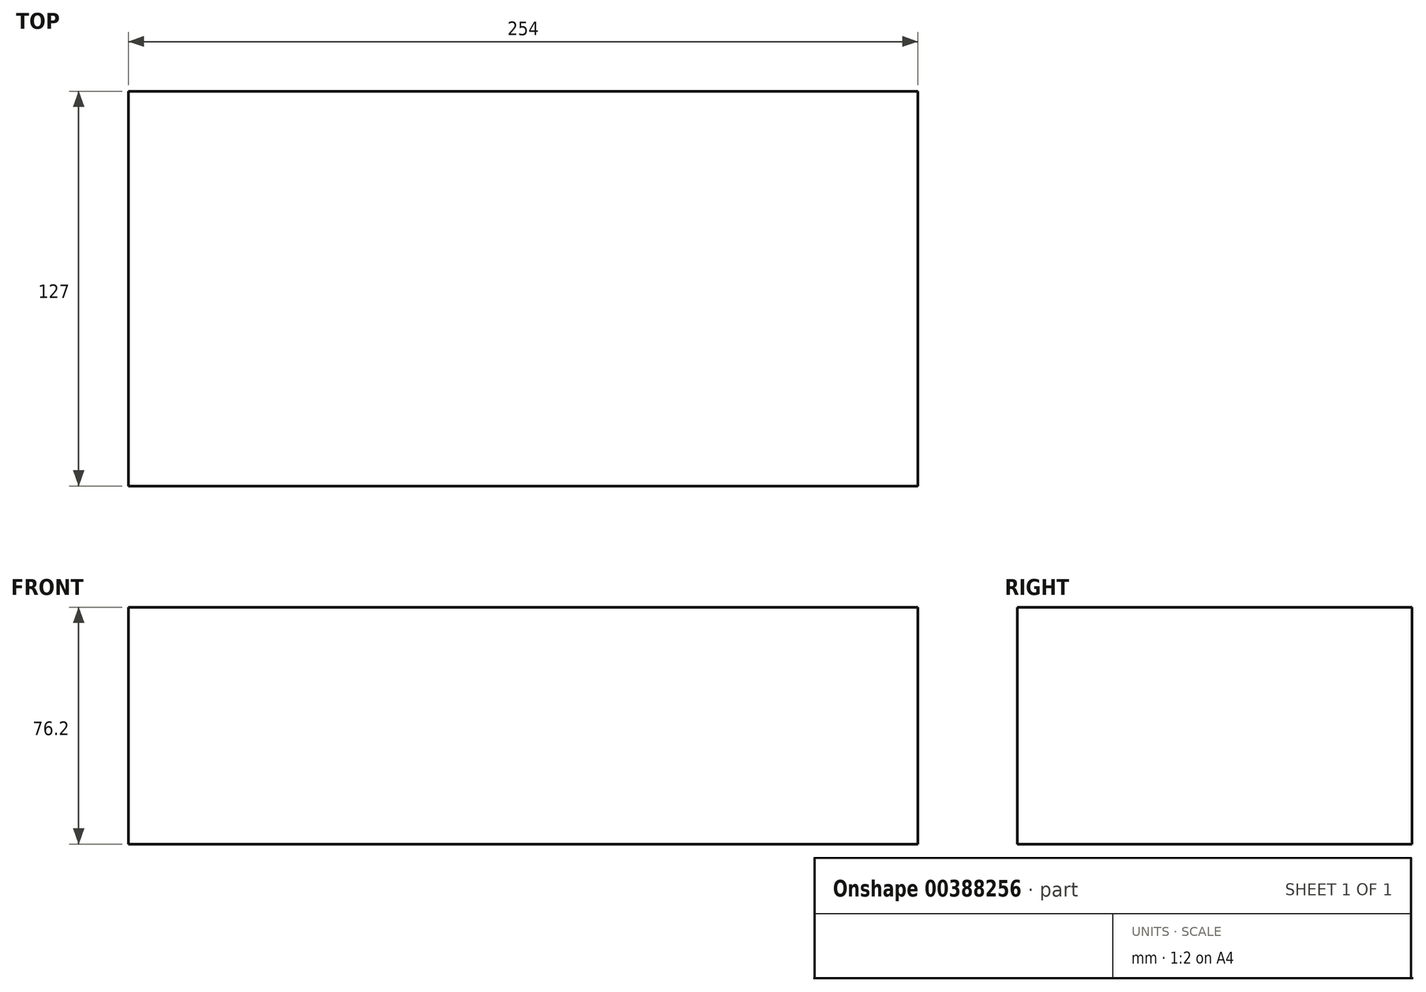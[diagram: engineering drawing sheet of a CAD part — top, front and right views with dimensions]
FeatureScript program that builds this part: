
annotation { "Feature Type Name" : "Feature", "Feature Type Description" : "" }
export const myFeature = defineFeature(function(context is Context, id is Id, definition is map)
    precondition{}
    {
        {
            var Q0;
            Q0=qCreatedBy(makeId("Top.planeOp"),FACE);
            var sketch = newSketch(context, id + "F0", { "sketchPlane" : qUnion([Q0])});
            skLineSegment(sketch, "E0.bottom", {"start": v(0, 0) * mm, "end": v(254, 0) * mm});
            skLineSegment(sketch, "E0.top", {"start": v(0, -127) * mm, "end": v(254, -127) * mm});
            skLineSegment(sketch, "E0.left", {"start": v(0, 0) * mm, "end": v(0, -127) * mm});
            skLineSegment(sketch, "E0.right", {"start": v(254, 0) * mm, "end": v(254, -127) * mm});
            skSolve(sketch);
        }
        {
            var Q0;
            Q0 = qSketchRegion(id + "F0", true);
            extrude(context, id + "F1", {"entities" : qUnion([Q0]), "depth" : 76.2 * mm});
        }
    });
